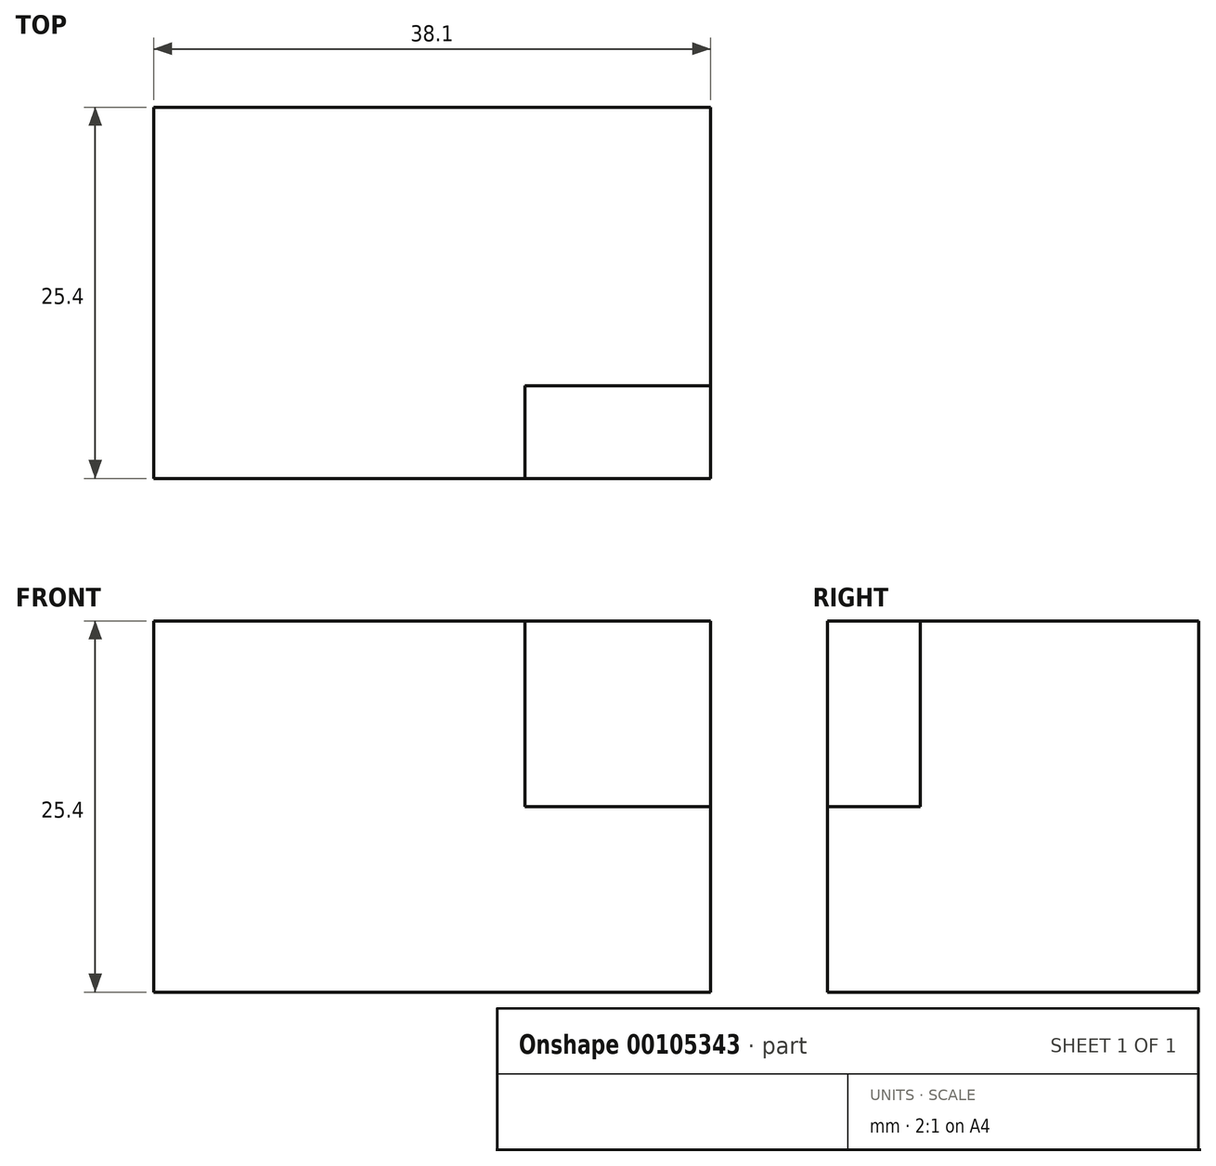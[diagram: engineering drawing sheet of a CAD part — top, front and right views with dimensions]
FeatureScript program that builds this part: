
annotation { "Feature Type Name" : "Feature", "Feature Type Description" : "" }
export const myFeature = defineFeature(function(context is Context, id is Id, definition is map)
    precondition{}
    {
        {
            var Q0;
            Q0=qCreatedBy(makeId("Front.planeOp"),FACE);
            var sketch = newSketch(context, id + "F0", { "sketchPlane" : qUnion([Q0])});
            skLineSegment(sketch, "E0.bottom", {"start": v(0, 0) * mm, "end": v(38.1, 0) * mm});
            skLineSegment(sketch, "E0.top", {"start": v(0, 25.4) * mm, "end": v(38.1, 25.4) * mm});
            skLineSegment(sketch, "E0.left", {"start": v(0, 0) * mm, "end": v(0, 25.4) * mm});
            skLineSegment(sketch, "E0.right", {"start": v(38.1, 0) * mm, "end": v(38.1, 25.4) * mm});
            skSolve(sketch);
        }
        {
            var Q0;
            Q0 = qSketchRegion(id + "F0", true);
            extrude(context, id + "F1", {"entities" : qUnion([Q0]), "endBound" : BoundingType.SYMMETRIC, "depth" : 25.4 * mm});
        }
        {
            var Q0;
            Q0=qCreatedBy(makeId("Front.planeOp"),FACE);
            var sketch = newSketch(context, id + "F2", { "sketchPlane" : qUnion([Q0])});
            skLineSegment(sketch, "E1.bottom", {"start": v(25.4, 25.4) * mm, "end": v(38.1, 25.4) * mm});
            skLineSegment(sketch, "E1.top", {"start": v(25.4, 12.7) * mm, "end": v(38.1, 12.7) * mm});
            skLineSegment(sketch, "E1.left", {"start": v(25.4, 25.4) * mm, "end": v(25.4, 12.7) * mm});
            skLineSegment(sketch, "E1.right", {"start": v(38.1, 25.4) * mm, "end": v(38.1, 12.7) * mm});
            skSolve(sketch);
        }
        {
            var Q0;
            Q0 = qSketchRegion(id + "F2", true);
            extrude(context, id + "F3", {"entities" : qUnion([Q0]), "operationType" : NewBodyOperationType.REMOVE, "depth" : 25.4 * mm, "hasSecondDirection" : true, "secondDirectionOppositeDirection" : false, "secondDirectionDepth" : 6.35 * mm});
        }
        {
            var Q0;
            Q0=qCreatedBy(makeId("Top.planeOp"),FACE);
            var sketch = newSketch(context, id + "F4", { "sketchPlane" : qUnion([Q0])});
            skLineSegment(sketch, "E2.bottom", {"start": v(0, 12.7) * mm, "end": v(12.7, 12.7) * mm});
            skLineSegment(sketch, "E2.top", {"start": v(0, 6.35) * mm, "end": v(12.7, 6.35) * mm});
            skLineSegment(sketch, "E2.left", {"start": v(0, 12.7) * mm, "end": v(0, 6.35) * mm});
            skLineSegment(sketch, "E2.right", {"start": v(12.7, 12.7) * mm, "end": v(12.7, 6.35) * mm});
            skLineSegment(sketch, "E3", {"start": v(0, 6.35) * mm, "end": v(25.4, -12.7) * mm});
            skLineSegment(sketch, "E4", {"start": v(12.7, 12.7) * mm, "end": v(38.1, -6.35) * mm});
            skSolve(sketch);
        }
        {
            var Q0;
            Q0 = qSketchRegion(id + "F4", true);
            extrude(context, id + "F5", {"entities" : qUnion([Q0]), "operationType" : NewBodyOperationType.REMOVE, "oppositeDirection" : true, "depth" : 25.4 * mm});
        }
    });
